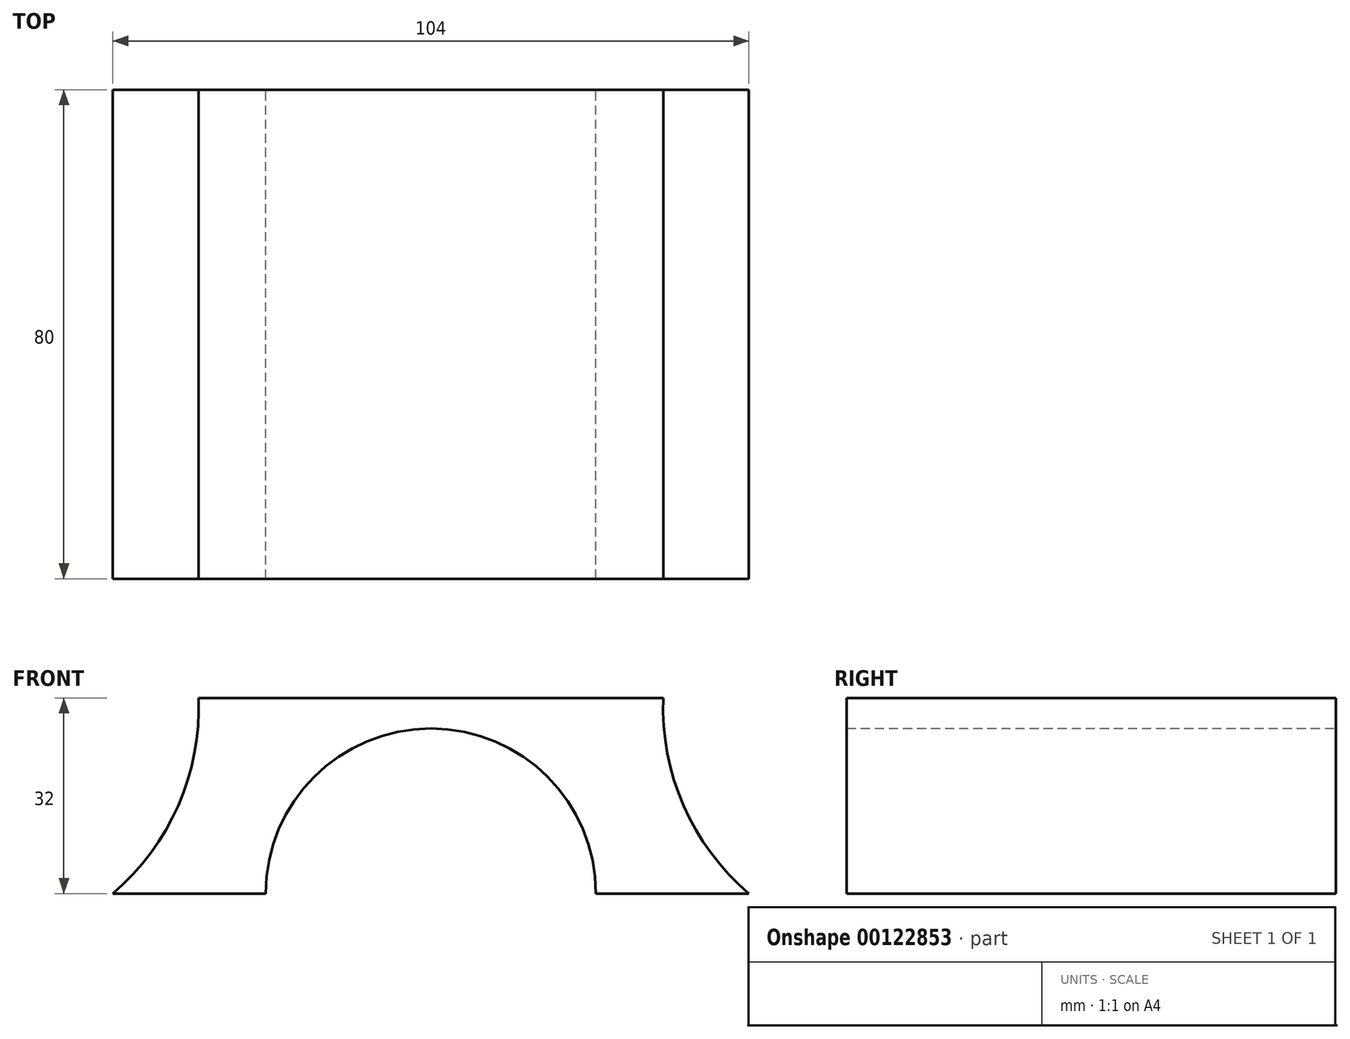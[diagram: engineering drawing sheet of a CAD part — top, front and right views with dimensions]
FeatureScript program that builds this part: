
annotation { "Feature Type Name" : "Feature", "Feature Type Description" : "" }
export const myFeature = defineFeature(function(context is Context, id is Id, definition is map)
    precondition{}
    {
        {
            var Q0;
            Q0=qCreatedBy(makeId("Front.planeOp"),FACE);
            var sketch = newSketch(context, id + "F0", { "sketchPlane" : qUnion([Q0])});
            skCircle(sketch, "E0", {"center": v(0, 0) * mm, "radius": 27 * mm, "construction": true});
            skArc(sketch, "E1", {"start": v(27, 0) * mm, "mid": v(0, 27) * mm, "end": v(-27, 0) * mm});
            skLineSegment(sketch, "E2", {"start": v(-27, 0) * mm, "end": v(-32, 0) * mm});
            skLineSegment(sketch, "E3", {"start": v(27, 0) * mm, "end": v(32, 0) * mm});
            skLineSegment(sketch, "E4", {"start": v(-32, 0) * mm, "end": v(-32, 5) * mm, "construction": true});
            skLineSegment(sketch, "E5", {"start": v(32, 0) * mm, "end": v(32, 5) * mm, "construction": true});
            skPoint(sketch, "E6.endSnap0", {"position": v(0, 27) * mm});
            skLineSegment(sketch, "E7", {"start": v(0, 27) * mm, "end": v(0, 32) * mm, "construction": true});
            skLineSegment(sketch, "E8", {"start": v(0, 32) * mm, "end": v(-38, 32) * mm});
            skLineSegment(sketch, "E9", {"start": v(0, 32) * mm, "end": v(38, 32) * mm});
            skArc(sketch, "E10", {"start": v(-52, 0) * mm, "mid": v(-41.32, 14.4) * mm, "end": v(-38, 32) * mm});
            skLineSegment(sketch, "E11", {"start": v(-52, 0) * mm, "end": v(-32, 0) * mm});
            skLineSegment(sketch, "E12", {"start": v(52, 0) * mm, "end": v(32, 0) * mm});
            skArc(sketch, "E13", {"start": v(38, 32) * mm, "mid": v(41.32, 14.4) * mm, "end": v(52, 0) * mm});
            skSolve(sketch);
        }
        {
            var Q0;
            Q0 = qSketchRegion(id + "F0", true);
            extrude(context, id + "F1", {"entities" : qUnion([Q0]), "depth" : 80 * mm});
        }
    });
